# Revit family: O3UD-NRG
name_source: partatom
category: Mechanical Equipment
units: mm (PartAtom-declared; Revit-internal decimal feet)

## family parameters
Always vertical = Yes
Cut with Voids When Loaded = No
OmniClass Number = 23.40.40.11.17
OmniClass Title = Refrigerated Cases
Part Type = Normal
Room Calculation Point = No
Round Connector Dimension = Use Radius
Shared = No
Work Plane-Based = Yes

## types (4) — shared parameters
12" Shelf = Yes
16" Shelf = Yes
20" Shelf = Yes
ANTI CON AMPS = 0 A
BOTTOM ELECTRICAL = Yes
BOTTOM REFRIGERATION PIPING = Yes
Certifications = NSF 7, UL471, CSA
DATE = 08/14/2018
DEFROST AMPS = 0 A
DESIGNERS NAME = SHIDDRAMESH
DISCHARGE AIR TEMP = 0 °F
DISCHARGE AIR VELOCITY = - (FPM)
DRAIN HEATERS AMPS = 0 A
DRAIN LINE CONNECTION = SANITARY CONNECTION
DRAIN LINE DIAMETER = 2"
DRAIN PIPE TYPE = PVC
DRAIN PIPING = Yes
DRIP PAN PLUMB TYPE = HARD
Default Elevation = 48"
Defrost Termination = - °F
Defrost Type = TIMED-OFF DEFROST
Description = O3UD-NRG
EQUIPMENT DESCRIPTION = O3UD-NRG
EQUIPMENT MARK = O3UD-NRG
GLASS = Glass
HIGH EFFICIENCY FANS AMPS = 0 A
Height = 48 1/16"
Item Description = O3UD-NRG
LF STD END = Yes
LIGHT AMPS = 0 A
LIQUID LINE CONNECTION = LIQUID LINE CONNECTION
LIQUID LINE DIAMETER = 0"
LIQUID LINE RADIUS = 0"
LOAD 1 CLASSIFICATION = Lighting
LOAD 1 DESCRIPTION = LIGHTS - STANDARD POWER (SHELF or CORNICE)
LOAD 1 PLUG TYPE = HARDWIRED
LOAD 1 POLES = 1
LOAD 1 VOLTAGE = 120 V
LOAD 1 WATTAGE = 0 W
LOAD 2 CLASSIFICATION = Motor
LOAD 2 DESCRIPTION = HIGH EFFICIENCY FANS CONNECTION
LOAD 2 PLUG TYPE = HARDWIRED
LOAD 2 POLES = 1
LOAD 2 VOLTAGE = 120 V
LOAD 2 WATTAGE = 0 W
LOAD 3 CLASSIFICATION = Power
LOAD 3 DESCRIPTION = ANTI-SWEAT CONNECTION
LOAD 3 PLUG TYPE = HARDWIRED
LOAD 3 POLES = 1
LOAD 3 VOLTAGE = 120 V
LOAD 3 WATTAGE = 0 W
LOAD 4 DESCRIPTION = DEFROST HEATER CONNECTION
LOAD 4 PLUG TYPE = HARDWIRED
LOAD 4 POLES = 1
LOAD 4 VOLTAGE = 208 V
LOAD 4 WATTAGE = 0 W
LOAD 5 DESCRIPTION = DRAIN HEATER CONNECTION
LOAD 5 PLUG TYPE = HARDWIRED
LOAD 5 POLES = 1
LOAD 5 VOLTAGE = 120 V
LOAD 5 WATTAGE = 0 W
Legend Number = O3UD-NRG
Manufacturer = HILL PHOENIX
Model = O3UD-NRG
PAINTED METAL UPPER SHELF = PAINTED SHELVES
POWER FACTOR = 1
PRESSURE REGULATOR = 0.00 psi
REFRIGERATION PIPING = COPPER PIPE
RT STD END = Yes
Refrig Charge Lbs = -
SANITARY PIPE SIZE = 1"
STAINLESS STEEL = GALVANIZED STEEL
SUCTION LINE CONNECTION = SUCTION LINE CONNECTION
SUCTION LINE DIAMETER = 1"
SUCTION LINE RADIUS = 0"
TOP ELECTRICAL = Yes
TOP REFRIGERATION PIPING = Yes
URL = http://www.hillphoenix.com
Width = 43 1/4"
zero-valued in all types: Defrost Num Day, Evap Temp, Load Mbh

## per-type parameters (varying)
| type | DRAIN LINE | Length | REAR REFRIGERATION |
| 8' | 48" | 96" | 28 5/8" |
| 4' | 36" | 48" | 22 3/4" |
| 6' | 36" | 72" | 28 5/8" |
| 12' | 72" | 144" | 28 5/8" |

## geometry (parser evidence)
native form markers: Blend x10, Sweep x2
no freeform markers — native parametric forms only
